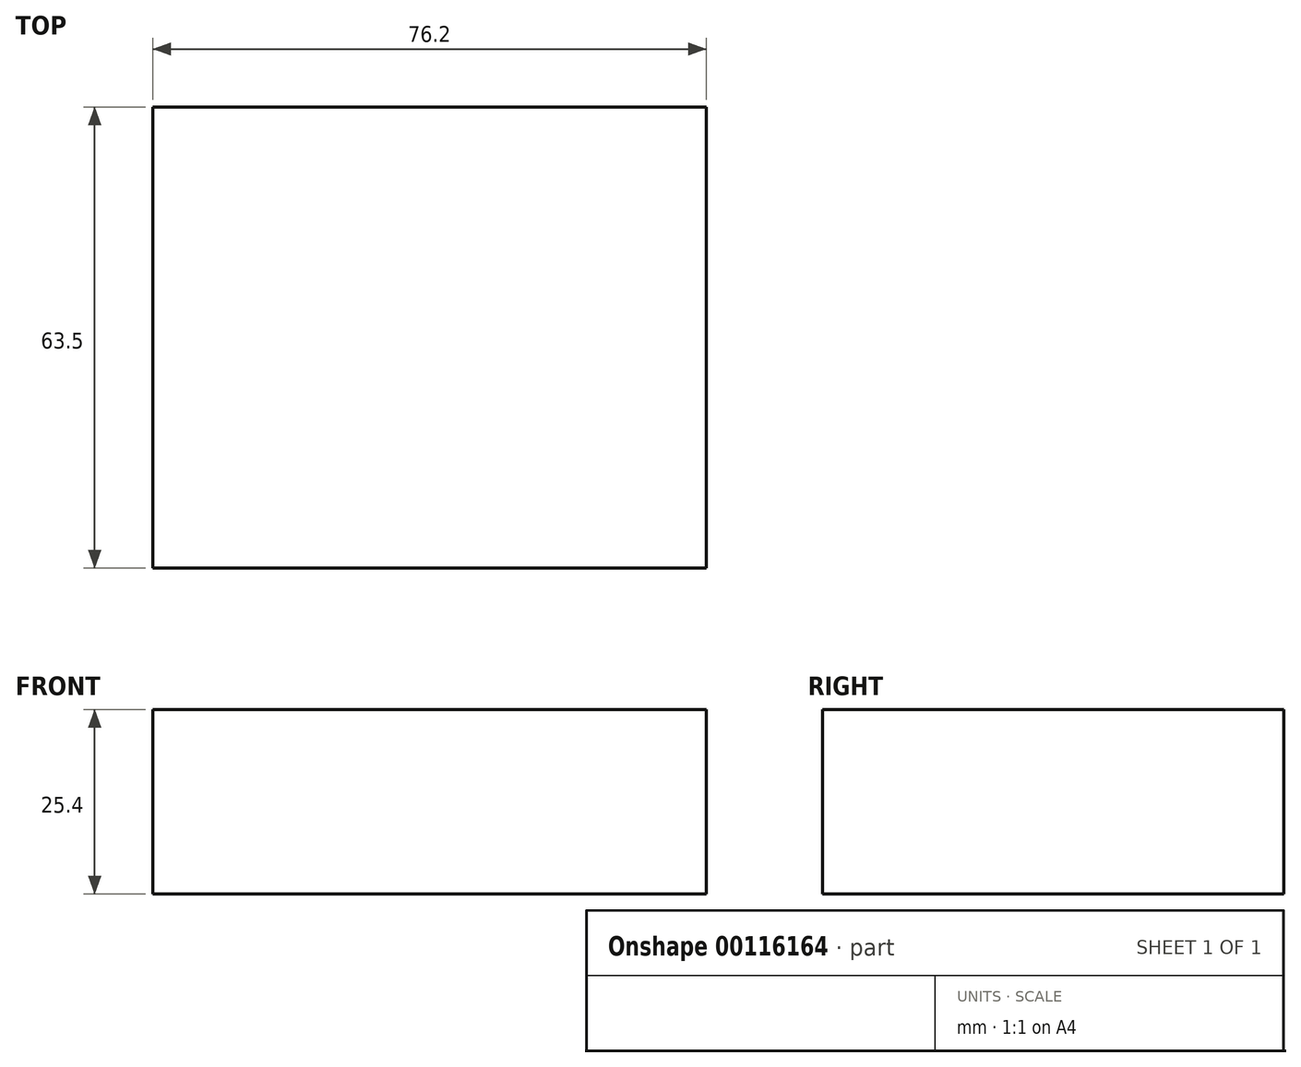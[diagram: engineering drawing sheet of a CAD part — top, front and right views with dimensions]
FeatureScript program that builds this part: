
annotation { "Feature Type Name" : "Feature", "Feature Type Description" : "" }
export const myFeature = defineFeature(function(context is Context, id is Id, definition is map)
    precondition{}
    {
        {
            var Q0;
            Q0=qCreatedBy(makeId("Top.planeOp"),FACE);
            var sketch = newSketch(context, id + "F0", { "sketchPlane" : qUnion([Q0])});
            skLineSegment(sketch, "E0.bottom", {"start": v(38.1, 31.75) * mm, "end": v(-38.1, 31.75) * mm});
            skLineSegment(sketch, "E0.top", {"start": v(38.1, -31.75) * mm, "end": v(-38.1, -31.75) * mm});
            skLineSegment(sketch, "E0.left", {"start": v(38.1, 31.75) * mm, "end": v(38.1, -31.75) * mm});
            skLineSegment(sketch, "E0.right", {"start": v(-38.1, 31.75) * mm, "end": v(-38.1, -31.75) * mm});
            skPoint(sketch, "E0.middle", {"position": v(0, 0) * mm});
            skSolve(sketch);
        }
        {
            var Q0;
            Q0=makeQuery(id+"F0.imprint","IMPRINT",FACE,{"disambiguationData":[TD([[makeQuery(id+"F0.imprint","IMPRINT",EDGE,{"derivedFrom":sQuery(id+"F0.wireOp",EDGE,"E0.bottom")}),1.0]])]});
            extrude(context, id + "F1", {"entities" : qUnion([Q0]), "depth" : 25.4 * mm});
        }
    });
